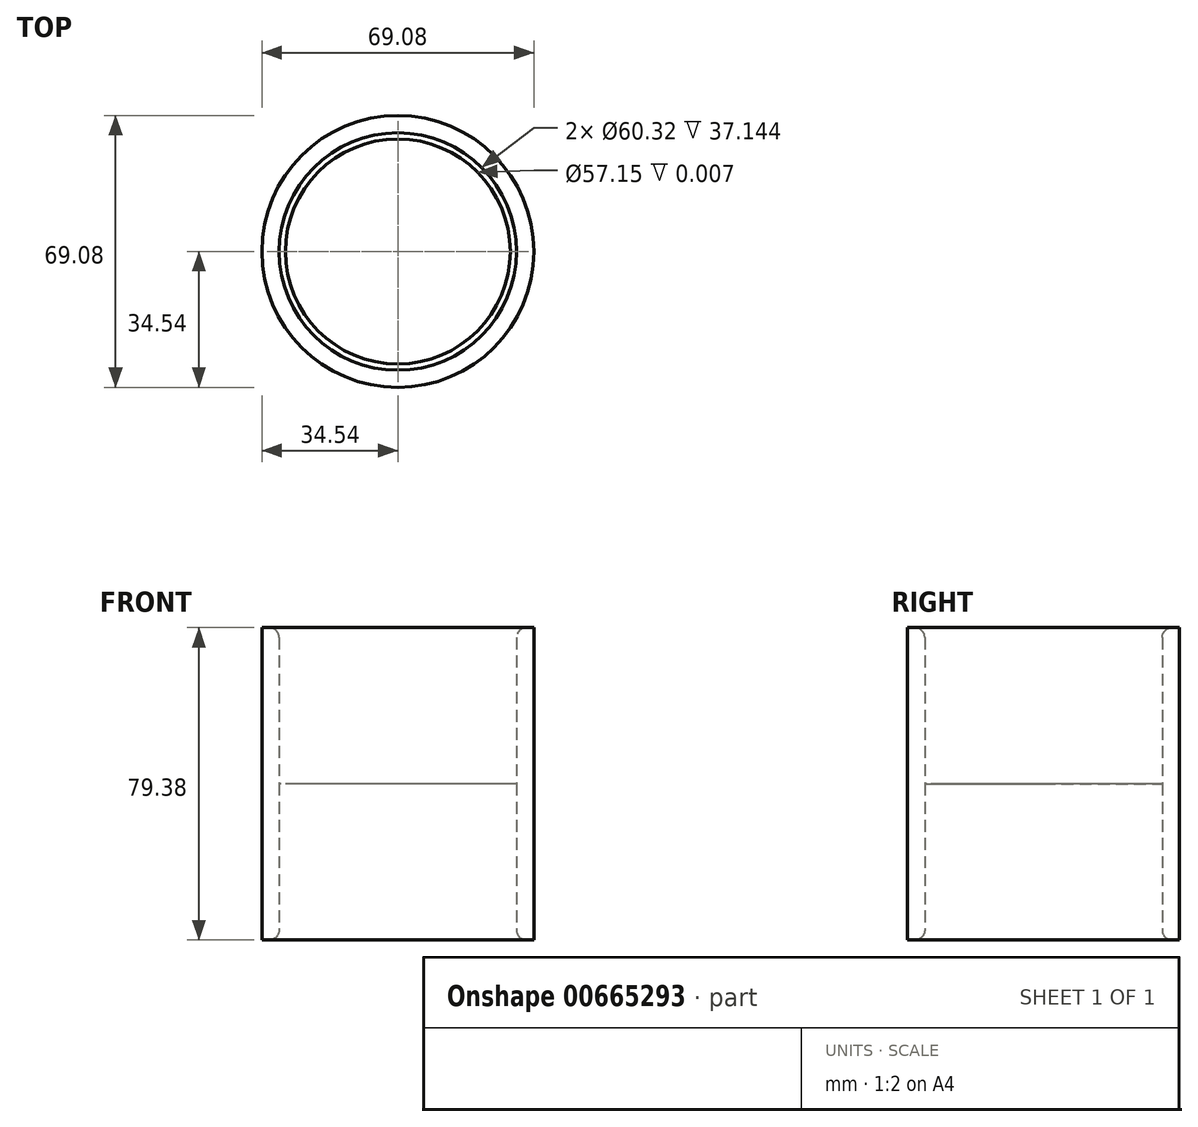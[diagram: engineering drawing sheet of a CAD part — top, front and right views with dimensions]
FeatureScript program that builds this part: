
annotation { "Feature Type Name" : "Feature", "Feature Type Description" : "" }
export const myFeature = defineFeature(function(context is Context, id is Id, definition is map)
    precondition{}
    {
        {
            var Q0;
            Q0=qCreatedBy(makeId("Top.planeOp"),FACE);
            var sketch = newSketch(context, id + "F0", { "sketchPlane" : qUnion([Q0])});
            skCircle(sketch, "E0", {"center": v(0, 0) * mm, "radius": 30.16 * mm});
            skCircle(sketch, "E1", {"center": v(0, 0) * mm, "radius": 34.54 * mm});
            skCircle(sketch, "E2", {"center": v(0, 0) * mm, "radius": 28.58 * mm});
            skSolve(sketch);
        }
        {
            var Q0;
            Q0=makeQuery(id+"F0.imprint","IMPRINT",FACE,{"disambiguationData":[TD([[makeQuery(id+"F0.imprint","IMPRINT",EDGE,{"derivedFrom":sQuery(id+"F0.wireOp",EDGE,"E0")}),-1.0]])]});
            extrude(context, id + "F1", {"entities" : qUnion([Q0]), "depth" : 79.38 * mm / 2, "hasSecondDirection" : true, "secondDirectionOppositeDirection" : true, "secondDirectionDepth" : 39.69 * mm});
        }
        {
            var Q0;
            Q0=makeQuery(id+"F0.imprint","IMPRINT",FACE,{"disambiguationData":[TD([[makeQuery(id+"F0.imprint","IMPRINT",EDGE,{"derivedFrom":sQuery(id+"F0.wireOp",EDGE,"E0")}),1.0]])]});
            extrude(context, id + "F2", {"entities" : qUnion([Q0]), "operationType" : NewBodyOperationType.ADD, "depth" : ((3.38 / 2) - 1.5) / 50.8 * mm, "hasSecondDirection" : true, "secondDirectionOppositeDirection" : true, "secondDirectionDepth" : ((3.38 / 2) - 1.5) / 50.8 * mm});
        }
        {
            var Q0;
            Q0=makeQuery(id+"F1.opExtrude","CAP_EDGE",EDGE,{"disambiguationData":[OSD([sQuery(id+"F0.wireOp",EDGE,"E0")])],"isStart":false});
            var Q1;
            Q1=makeQuery(id+"F1.opExtrude","CAP_EDGE",EDGE,{"disambiguationData":[OSD([sQuery(id+"F0.wireOp",EDGE,"E0")])],"isStart":true});
            fillet(context, id + "F3", {"entities" : qUnion([Q0, Q1]), "radius" : 2.54 * mm, "tangentPropagation" : true, "allowEdgeOverflow" : false});
        }
    });
